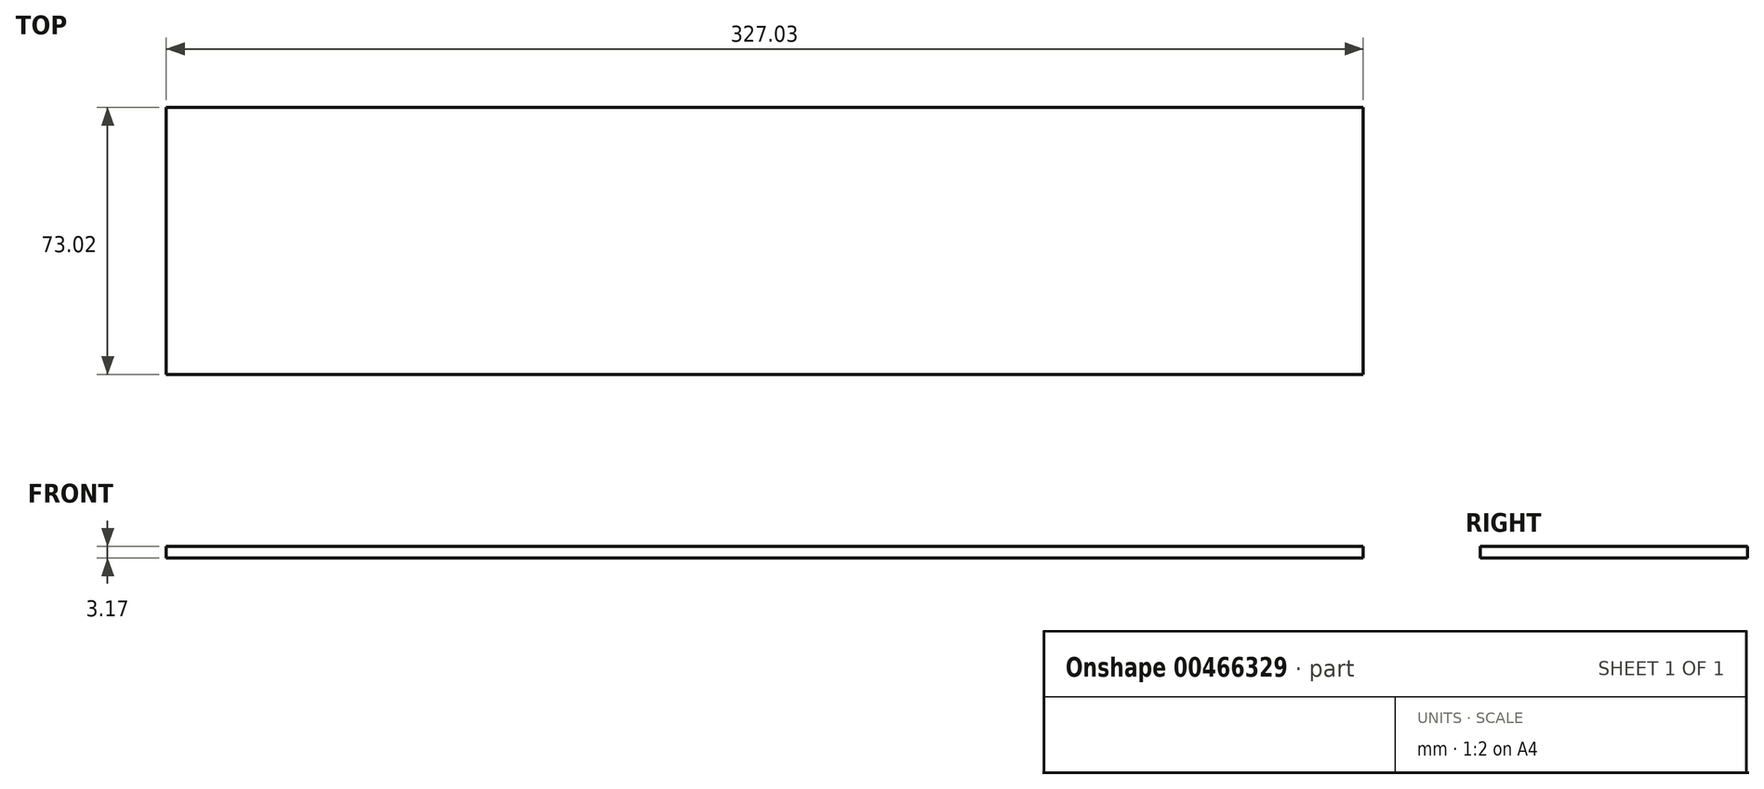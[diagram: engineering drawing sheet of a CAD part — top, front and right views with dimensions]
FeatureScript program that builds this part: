
annotation { "Feature Type Name" : "Feature", "Feature Type Description" : "" }
export const myFeature = defineFeature(function(context is Context, id is Id, definition is map)
    precondition{}
    {
        {
            var Q0;
            Q0=qCreatedBy(makeId("Top.planeOp"),FACE);
            var sketch = newSketch(context, id + "F0", { "sketchPlane" : qUnion([Q0])});
            skLineSegment(sketch, "E0.bottom", {"start": v(-168.4, 4.5) * mm, "end": v(158.62, 4.5) * mm});
            skLineSegment(sketch, "E0.top", {"start": v(-168.4, -68.52) * mm, "end": v(158.62, -68.52) * mm});
            skLineSegment(sketch, "E0.left", {"start": v(-168.4, 4.5) * mm, "end": v(-168.4, -68.52) * mm});
            skLineSegment(sketch, "E0.right", {"start": v(158.62, 4.5) * mm, "end": v(158.62, -68.52) * mm});
            skSolve(sketch);
        }
        {
            var Q0;
            Q0 = qSketchRegion(id + "F0", true);
            extrude(context, id + "F1", {"entities" : qUnion([Q0]), "depth" : 3.17 * mm});
        }
    });
